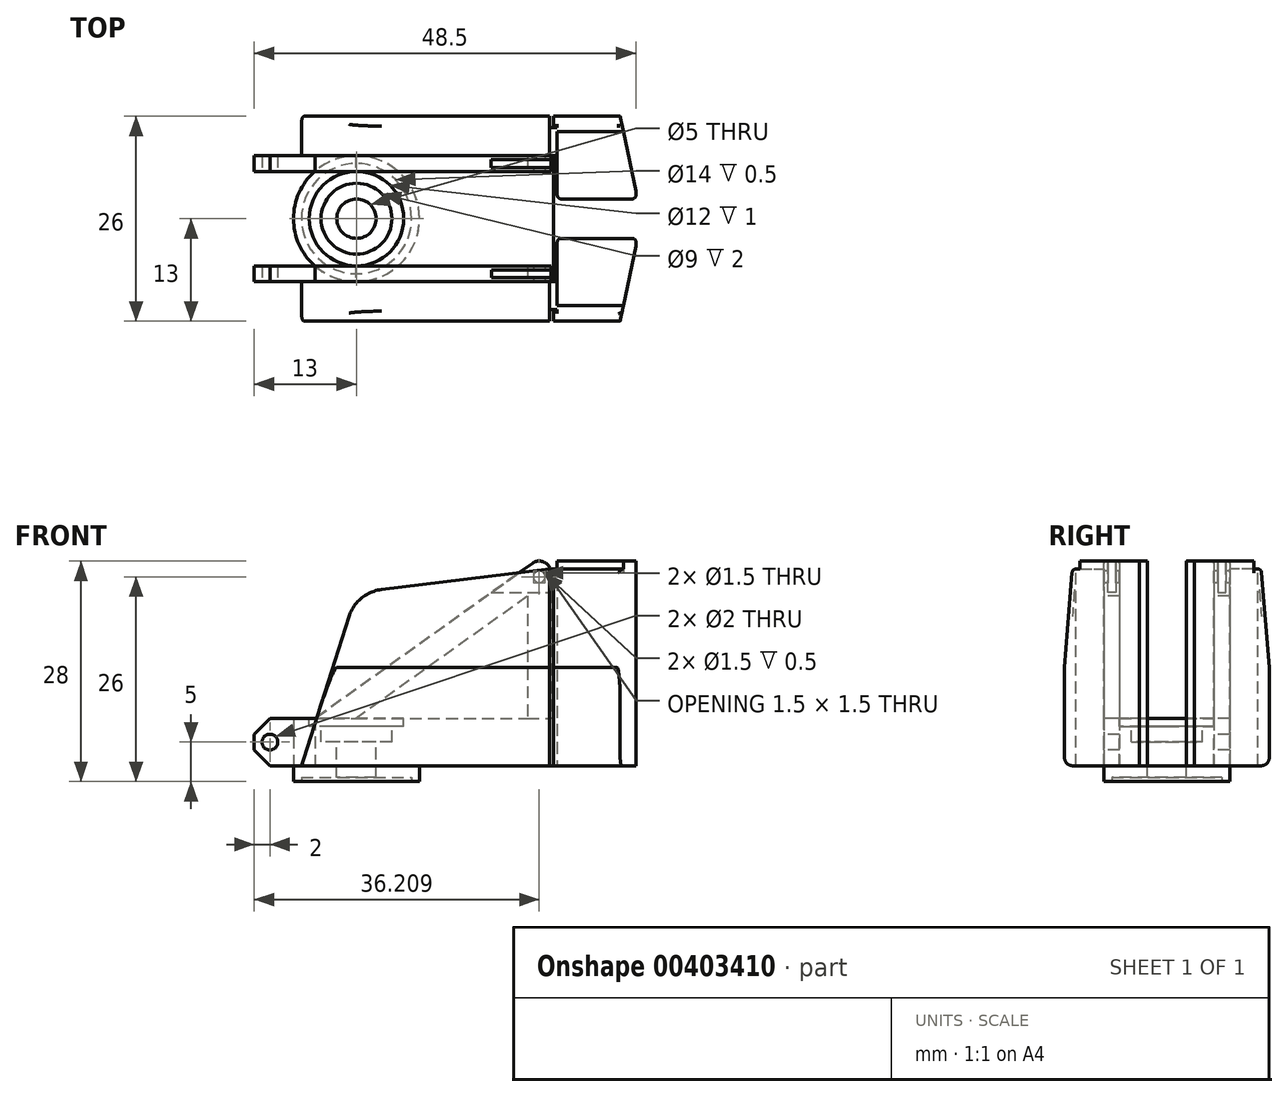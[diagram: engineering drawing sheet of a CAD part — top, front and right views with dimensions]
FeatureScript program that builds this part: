
annotation { "Feature Type Name" : "Feature", "Feature Type Description" : "" }
export const myFeature = defineFeature(function(context is Context, id is Id, definition is map)
    precondition{}
    {
        {
            var Q0;
            Q0=qCreatedBy(makeId("Top.planeOp"),FACE);
            var sketch = newSketch(context, id + "F0", { "sketchPlane" : qUnion([Q0])});
            skCircle(sketch, "E0", {"center": v(0, 0) * mm, "radius": 8 * mm});
            skSolve(sketch);
        }
        {
            var Q0;
            Q0 = qSketchRegion(id + "F0", true);
            extrude(context, id + "F1", {"entities" : qUnion([Q0]), "depth" : 2 * mm});
        }
        {
            var Q0;
            Q0=makeQuery(id+"F1.opExtrude","CAP_FACE",FACE,{"disambiguationData":[OSD([sQuery(id+"F0.wireOp",EDGE,"E0")])],"isStart":true});
            var sketch = newSketch(context, id + "F2", { "sketchPlane" : qUnion([Q0])});
            skCircle(sketch, "E1", {"center": v(0, 0) * mm, "radius": 7 * mm});
            skSolve(sketch);
        }
        {
            var Q0;
            Q0 = qSketchRegion(id + "F2", true);
            extrude(context, id + "F3", {"entities" : qUnion([Q0]), "operationType" : NewBodyOperationType.REMOVE, "oppositeDirection" : true, "depth" : 0.5 * mm});
        }
        {
            var Q0;
            Q0=makeQuery(id+"F1.opExtrude","CAP_FACE",FACE,{"disambiguationData":[OSD([sQuery(id+"F0.wireOp",EDGE,"E0")])],"isStart":false});
            var sketch = newSketch(context, id + "F4", { "sketchPlane" : qUnion([Q0])});
            skLineSegment(sketch, "E2", {"start": v(0, 0) * mm, "end": v(0, 6) * mm, "construction": true});
            skLineSegment(sketch, "E3.MirrorCS", {"start": v(0, 0) * mm, "end": v(0, -6) * mm, "construction": true});
            skLineSegment(sketch, "E4", {"start": v(-8, 0) * mm, "end": v(-13, 0) * mm, "construction": true});
            skLineSegment(sketch, "E5", {"start": v(-5.3, 6) * mm, "end": v(-13, 6) * mm});
            skLineSegment(sketch, "E6", {"start": v(-13, 6) * mm, "end": v(-13, 8) * mm});
            skLineSegment(sketch, "E7", {"start": v(-13, 8) * mm, "end": v(0, 8) * mm});
            skLineSegment(sketch, "E8", {"start": v(0, 8) * mm, "end": v(0, 6) * mm});
            skLineSegment(sketch, "E9.MirrorCS", {"start": v(-5.3, -6) * mm, "end": v(-13, -6) * mm});
            skLineSegment(sketch, "E10.MirrorCS", {"start": v(-13, -6) * mm, "end": v(-13, -8) * mm});
            skLineSegment(sketch, "E11.MirrorCS", {"start": v(-13, -8) * mm, "end": v(0, -8) * mm});
            skLineSegment(sketch, "E12.MirrorCS", {"start": v(0, -8) * mm, "end": v(0, -6) * mm});
            skArc(sketch, "E13", {"start": v(-5.3, -6) * mm, "mid": v(-8, 0) * mm, "end": v(-5.3, 6) * mm});
            skPoint(sketch, "E14.orphan", {"position": v(0, -6) * mm});
            skArc(sketch, "E15", {"start": v(0, -8) * mm, "mid": v(8, 0) * mm, "end": v(0, 8) * mm});
            skLineSegment(sketch, "E16", {"start": v(0, 8) * mm, "end": v(25, 8) * mm});
            skLineSegment(sketch, "E17", {"start": v(25, 8) * mm, "end": v(25, -8) * mm});
            skLineSegment(sketch, "E18", {"start": v(25, -8) * mm, "end": v(0, -8) * mm});
            skSolve(sketch);
        }
        {
            var Q0;
            Q0 = qSketchRegion(id + "F4", true);
            extrude(context, id + "F5", {"entities" : qUnion([Q0]), "operationType" : NewBodyOperationType.ADD, "depth" : 6 * mm});
        }
        {
            var Q0;
            Q0=makeQuery(id+"F5.opExtrude","SWEPT_FACE",FACE,{"disambiguationData":[OSD([sQuery(id+"F4.wireOp",EDGE,"E11.MirrorCS"),sQuery(id+"F4.wireOp",EDGE,"E18")])]});
            var sketch = newSketch(context, id + "F6", { "sketchPlane" : qUnion([Q0])});
            skLineSegment(sketch, "E19", {"start": v(-13, 5) * mm, "end": v(-11, 5) * mm, "construction": true});
            skCircle(sketch, "E20", {"center": v(-11, 5) * mm, "radius": 1 * mm});
            skLineSegment(sketch, "E21", {"start": v(-13, 6) * mm, "end": v(-9.76, 6) * mm, "construction": true});
            skLineSegment(sketch, "E22", {"start": v(-11, 8) * mm, "end": v(-13, 6) * mm});
            skLineSegment(sketch, "E23.MirrorCS", {"start": v(-11, 2) * mm, "end": v(-13, 4) * mm});
            skSolve(sketch);
        }
        {
            var Q0;
            {var subQ0=sQuery(id+"F6.wireOp",EDGE,"E22");Q0=makeQuery(id+"F6.imprint","IMPRINT",FACE,{"disambiguationData":[TD([[makeQuery(id+"F6.imprint","IMPRINT",EDGE,{"derivedFrom":subQ0}),-1.0]])]});}
            var Q1;
            {var subQ0=sQuery(id+"F6.wireOp",EDGE,"E23.MirrorCS");Q1=makeQuery(id+"F6.imprint","IMPRINT",FACE,{"disambiguationData":[TD([[makeQuery(id+"F6.imprint","IMPRINT",EDGE,{"derivedFrom":subQ0}),1.0]])]});}
            var Q2;
            Q2=makeQuery(id+"F6.imprint","IMPRINT",FACE,{"disambiguationData":[TD([[makeQuery(id+"F6.imprint","IMPRINT",EDGE,{"derivedFrom":sQuery(id+"F6.wireOp",EDGE,"E20")}),1.0]])]});
            extrude(context, id + "F7", {"entities" : qUnion([Q0, Q1, Q2]), "operationType" : NewBodyOperationType.REMOVE, "oppositeDirection" : true, "depth" : 25 * mm});
        }
        {
            var Q0;
            Q0=makeQuery(id+"F5.opExtrude","CAP_FACE",FACE,{"disambiguationData":[OSD([sQuery(id+"F4.wireOp",EDGE,"E5"),sQuery(id+"F4.wireOp",EDGE,"E6"),sQuery(id+"F4.wireOp",EDGE,"E7"),sQuery(id+"F4.wireOp",EDGE,"E9.MirrorCS"),sQuery(id+"F4.wireOp",EDGE,"E10.MirrorCS"),sQuery(id+"F4.wireOp",EDGE,"E11.MirrorCS"),sQuery(id+"F4.wireOp",EDGE,"E13"),sQuery(id+"F4.wireOp",EDGE,"E16"),sQuery(id+"F4.wireOp",EDGE,"E17"),sQuery(id+"F4.wireOp",EDGE,"E18")])],"isStart":false});
            var sketch = newSketch(context, id + "F8", { "sketchPlane" : qUnion([Q0])});
            skCircle(sketch, "E24", {"center": v(0, 0) * mm, "radius": 6 * mm});
            skSolve(sketch);
        }
        {
            var Q0;
            Q0=makeQuery(id+"F8.imprint","IMPRINT",FACE,{"disambiguationData":[TD([[makeQuery(id+"F8.imprint","IMPRINT",EDGE,{"derivedFrom":sQuery(id+"F8.wireOp",EDGE,"E24")}),1.0]])]});
            extrude(context, id + "F9", {"entities" : qUnion([Q0]), "operationType" : NewBodyOperationType.REMOVE, "oppositeDirection" : true, "depth" : 1 * mm});
        }
        {
            var Q0;
            Q0=makeQuery(id+"F9.boolean.opBoolean","COPY",FACE,{"derivedFrom":makeQuery(id+"F9.opExtrude","CAP_FACE",FACE,{"disambiguationData":[OSD([sQuery(id+"F8.wireOp",EDGE,"E24")])],"isStart":false})});
            var sketch = newSketch(context, id + "F10", { "sketchPlane" : qUnion([Q0])});
            skCircle(sketch, "E25", {"center": v(0, 0) * mm, "radius": 2.5 * mm});
            skSolve(sketch);
        }
        {
            var Q0;
            Q0=makeQuery(id+"F10.imprint","IMPRINT",FACE,{"disambiguationData":[TD([[makeQuery(id+"F10.imprint","IMPRINT",EDGE,{"derivedFrom":sQuery(id+"F10.wireOp",EDGE,"E25")}),1.0]])]});
            extrude(context, id + "F11", {"entities" : qUnion([Q0]), "operationType" : NewBodyOperationType.REMOVE, "oppositeDirection" : true, "depth" : 25 * mm});
        }
        {
            var Q0;
            Q0=makeQuery(id+"F5.opExtrude","CAP_FACE",FACE,{"disambiguationData":[OSD([sQuery(id+"F4.wireOp",EDGE,"E5"),sQuery(id+"F4.wireOp",EDGE,"E6"),sQuery(id+"F4.wireOp",EDGE,"E7"),sQuery(id+"F4.wireOp",EDGE,"E9.MirrorCS"),sQuery(id+"F4.wireOp",EDGE,"E10.MirrorCS"),sQuery(id+"F4.wireOp",EDGE,"E11.MirrorCS"),sQuery(id+"F4.wireOp",EDGE,"E13"),sQuery(id+"F4.wireOp",EDGE,"E16"),sQuery(id+"F4.wireOp",EDGE,"E17"),sQuery(id+"F4.wireOp",EDGE,"E18")])],"isStart":false});
            var sketch = newSketch(context, id + "F12", { "sketchPlane" : qUnion([Q0])});
            skLineSegment(sketch, "E26", {"start": v(-5.3, 6) * mm, "end": v(24.7, 6) * mm});
            skLineSegment(sketch, "E27", {"start": v(-5.3, 6) * mm, "end": v(-5.3, 8) * mm});
            skLineSegment(sketch, "E28", {"start": v(-5.3, 8) * mm, "end": v(24.7, 8) * mm});
            skLineSegment(sketch, "E29", {"start": v(24.7, 8) * mm, "end": v(24.7, 6) * mm});
            skLineSegment(sketch, "E30.MirrorCS", {"start": v(-5.3, -6) * mm, "end": v(24.7, -6) * mm});
            skLineSegment(sketch, "E31.MirrorCS", {"start": v(-5.3, -6) * mm, "end": v(-5.3, -8) * mm});
            skLineSegment(sketch, "E32.MirrorCS", {"start": v(-5.3, -8) * mm, "end": v(24.7, -8) * mm});
            skLineSegment(sketch, "E33.MirrorCS", {"start": v(24.7, -8) * mm, "end": v(24.7, -6) * mm});
            skSolve(sketch);
        }
        {
            var Q0;
            {var subQ0=sQuery(id+"F12.wireOp",EDGE,"E27");Q0=makeQuery(id+"F12.imprint","IMPRINT",FACE,{"disambiguationData":[TD([[makeQuery(id+"F12.imprint","IMPRINT",EDGE,{"derivedFrom":subQ0}),-1.0]])]});}
            var Q1;
            {var subQ0=sQuery(id+"F12.wireOp",EDGE,"E31.MirrorCS");Q1=makeQuery(id+"F12.imprint","IMPRINT",FACE,{"disambiguationData":[TD([[makeQuery(id+"F12.imprint","IMPRINT",EDGE,{"derivedFrom":subQ0}),1.0]])]});}
            extrude(context, id + "F13", {"entities" : qUnion([Q0, Q1]), "operationType" : NewBodyOperationType.ADD, "depth" : 20 * mm});
        }
        {
            var Q0;
            Q0=makeQuery(id+"F13.boolean.opBoolean","MERGE",FACE,{"derivedFrom":[makeQuery(id+"F5.opExtrude","SWEPT_FACE",FACE,{"disambiguationData":[OSD([sQuery(id+"F4.wireOp",EDGE,"E11.MirrorCS"),sQuery(id+"F4.wireOp",EDGE,"E18")])]}),makeQuery(id+"F13.opExtrude","SWEPT_FACE",FACE,{"disambiguationData":[OSD([sQuery(id+"F12.wireOp",EDGE,"E32.MirrorCS")])]})]});
            var sketch = newSketch(context, id + "F14", { "sketchPlane" : qUnion([Q0])});
            skLineSegment(sketch, "E34", {"start": v(24.7, 28) * mm, "end": v(21.7, 28) * mm, "construction": true});
            skLineSegment(sketch, "E35", {"start": v(23.2, 28) * mm, "end": v(23.2, 26.5) * mm, "construction": true});
            skArc(sketch, "E36", {"start": v(24.7, 26.5) * mm, "mid": v(23.9, 27.83) * mm, "end": v(22.34, 27.72) * mm});
            skLineSegment(sketch, "E37", {"start": v(-5.3, 8) * mm, "end": v(22.34, 27.72) * mm});
            skPoint(sketch, "E37.endSnap0", {"position": v(22.34, 27.72) * mm});
            skLineSegment(sketch, "E38", {"start": v(-5.3, 8) * mm, "end": v(24.7, 8) * mm, "construction": true});
            skLineSegment(sketch, "E39", {"start": v(21.7, 23.59) * mm, "end": v(-0.13, 8) * mm});
            skLineSegment(sketch, "E40", {"start": v(21.7, 8) * mm, "end": v(21.7, 23.59) * mm});
            skLineSegment(sketch, "E41", {"start": v(23.2, 26.5) * mm, "end": v(23.2, 26) * mm, "construction": true});
            skCircle(sketch, "E42", {"center": v(23.2, 26) * mm, "radius": 0.75 * mm});
            skLineSegment(sketch, "E43", {"start": v(-0.13, 8) * mm, "end": v(21.7, 8) * mm});
            skSolve(sketch);
        }
        {
            var Q0;
            {var subQ0=sQuery(id+"F14.wireOp",EDGE,"E37");Q0=makeQuery(id+"F14.imprint","IMPRINT",FACE,{"disambiguationData":[TD([[makeQuery(id+"F14.imprint","IMPRINT",EDGE,{"derivedFrom":subQ0}),1.0]])]});}
            var Q1;
            Q1=makeQuery(id+"F14.imprint","IMPRINT",FACE,{"disambiguationData":[TD([[makeQuery(id+"F14.imprint","IMPRINT",EDGE,{"derivedFrom":sQuery(id+"F14.wireOp",EDGE,"E39")}),1.0]])]});
            var Q2;
            Q2=makeQuery(id+"F14.imprint","IMPRINT",FACE,{"disambiguationData":[TD([[makeQuery(id+"F14.imprint","IMPRINT",EDGE,{"derivedFrom":sQuery(id+"F14.wireOp",EDGE,"E42")}),1.0]])]});
            var Q3;
            {var subQ0=sQuery(id+"F14.wireOp",EDGE,"E36");var subQ1=sQuery(id+"F12.wireOp",EDGE,"E32.MirrorCS");var subQ4=makeQuery(id+"F13.opExtrude","CAP_EDGE",EDGE,{"disambiguationData":[OSD([subQ1])],"isStart":false});var subQ5=makeQuery(id+"F14.imprint","INTERSECT",VERTEX,{"derivedFrom":[subQ4,subQ0]});Q3=makeQuery(id+"F14.imprint","IMPRINT",FACE,{"disambiguationData":[TD([[makeQuery(id+"F14.imprint","IMPRINT",EDGE,{"disambiguationData":[TD([[subQ5,1.0]])],"derivedFrom":subQ0}),-1.0]])]});}
            extrude(context, id + "F15", {"entities" : qUnion([Q0, Q1, Q2, Q3]), "operationType" : NewBodyOperationType.REMOVE, "oppositeDirection" : true, "depth" : 25 * mm});
        }
        {
            var Q0;
            {var subQ0=sQuery(id+"F4.wireOp",EDGE,"E18");var subQ1=sQuery(id+"F4.wireOp",EDGE,"E11.MirrorCS");var subQ2=sQuery(id+"F4.wireOp",EDGE,"E16");var subQ3=sQuery(id+"F4.wireOp",EDGE,"E7");var subQ4=sQuery(id+"F4.wireOp",EDGE,"E17");var subQ5=sQuery(id+"F4.wireOp",EDGE,"E13");var subQ6=makeQuery(id+"F5.opExtrude","CAP_FACE",FACE,{"disambiguationData":[OSD([sQuery(id+"F4.wireOp",EDGE,"E5"),sQuery(id+"F4.wireOp",EDGE,"E6"),subQ3,sQuery(id+"F4.wireOp",EDGE,"E9.MirrorCS"),sQuery(id+"F4.wireOp",EDGE,"E10.MirrorCS"),subQ1,subQ5,subQ2,subQ4,subQ0])],"isStart":true});Q0=makeQuery(id+"F5.boolean.opBoolean","SPLIT",FACE,{"disambiguationData":[TD([makeQuery(id+"F5.opExtrude","SWEPT_FACE",FACE,{"disambiguationData":[OSD([subQ4])]})])],"derivedFrom":subQ6});}
            var sketch = newSketch(context, id + "F16", { "sketchPlane" : qUnion([Q0])});
            skLineSegment(sketch, "E44", {"start": v(0, 0) * mm, "end": v(-7, 0) * mm, "construction": true});
            skPoint(sketch, "E44.endSnap0", {"position": v(8, 0) * mm});
            skLineSegment(sketch, "E45", {"start": v(-7, 0) * mm, "end": v(-7, 8) * mm, "construction": true});
            skLineSegment(sketch, "E46", {"start": v(-7, 8) * mm, "end": v(-7, 13) * mm});
            skLineSegment(sketch, "E47", {"start": v(-7, 13) * mm, "end": v(24.5, 13) * mm});
            skLineSegment(sketch, "E48", {"start": v(24.5, 13) * mm, "end": v(24.5, 8) * mm});
            skLineSegment(sketch, "E49", {"start": v(24.5, 8) * mm, "end": v(-7, 8) * mm});
            skLineSegment(sketch, "E50.MirrorCS", {"start": v(24.5, -8) * mm, "end": v(-7, -8) * mm});
            skLineSegment(sketch, "E51.MirrorCS", {"start": v(-7, -8) * mm, "end": v(-7, -13) * mm});
            skLineSegment(sketch, "E52.MirrorCS", {"start": v(-7, -13) * mm, "end": v(24.5, -13) * mm});
            skLineSegment(sketch, "E53.MirrorCS", {"start": v(24.5, -13) * mm, "end": v(24.5, -8) * mm});
            skSolve(sketch);
        }
        {
            var Q0;
            Q0 = qSketchRegion(id + "F16", true);
            extrude(context, id + "F17", {"entities" : qUnion([Q0]), "operationType" : NewBodyOperationType.ADD, "oppositeDirection" : true, "depth" : 25 * mm});
        }
        {
            var Q0;
            Q0=makeQuery(id+"F17.opExtrude","SWEPT_FACE",FACE,{"disambiguationData":[OSD([sQuery(id+"F16.wireOp",EDGE,"E47")])]});
            var sketch = newSketch(context, id + "F18", { "sketchPlane" : qUnion([Q0])});
            skLineSegment(sketch, "E54", {"start": v(-7, 2) * mm, "end": v(-0.97, 20.94) * mm});
            skLineSegment(sketch, "E55", {"start": v(3.18, 24.39) * mm, "end": v(24.5, 27) * mm});
            skLineSegment(sketch, "E56", {"start": v(0, 27) * mm, "end": v(0, 24) * mm, "construction": true});
            skPoint(sketch, "E57.visualSharp", {"position": v(0, 24) * mm});
            skArc(sketch, "E57.filletArc", {"start": v(3.18, 24.39) * mm, "mid": v(0.6, 23.28) * mm, "end": v(-0.97, 20.94) * mm});
            skSolve(sketch);
        }
        {
            var Q0;
            Q0=makeQuery(id+"F18.imprint","IMPRINT",FACE,{"disambiguationData":[TD([[makeQuery(id+"F18.imprint","IMPRINT",EDGE,{"derivedFrom":sQuery(id+"F18.wireOp",EDGE,"E54")}),1.0]])]});
            extrude(context, id + "F19", {"entities" : qUnion([Q0]), "operationType" : NewBodyOperationType.REMOVE, "oppositeDirection" : true, "depth" : 5 * mm});
        }
        {
            var Q0;
            Q0=makeQuery(id+"F17.opExtrude","SWEPT_FACE",FACE,{"disambiguationData":[OSD([sQuery(id+"F16.wireOp",EDGE,"E48")])]});
            var sketch = newSketch(context, id + "F20", { "sketchPlane" : qUnion([Q0])});
            skLineSegment(sketch, "E58", {"start": v(-13, 14.5) * mm, "end": v(-12, 27) * mm});
            skLineSegment(sketch, "E59", {"start": v(-12, 27) * mm, "end": v(-8, 27) * mm});
            skSolve(sketch);
        }
        {
            var Q0;
            {var subQ0=sQuery(id+"F20.wireOp",EDGE,"E58");Q0=makeQuery(id+"F20.imprint","IMPRINT",FACE,{"disambiguationData":[TD([[makeQuery(id+"F20.imprint","IMPRINT",EDGE,{"derivedFrom":subQ0}),1.0]])]});}
            extrude(context, id + "F21", {"entities" : qUnion([Q0]), "operationType" : NewBodyOperationType.REMOVE, "oppositeDirection" : true, "depth" : 30 * mm});
        }
        {
            var Q0;
            Q0=makeQuery(id+"F21.boolean.opBoolean","INTERSECT",EDGE,{"derivedFrom":[makeQuery(id+"F19.boolean.opBoolean","COPY",FACE,{"derivedFrom":makeQuery(id+"F19.opExtrude","SWEPT_FACE",FACE,{"disambiguationData":[OSD([sQuery(id+"F18.wireOp",EDGE,"E55")])]})}),makeQuery(id+"F21.opExtrude","SWEPT_FACE",FACE,{"disambiguationData":[OSD([sQuery(id+"F20.wireOp",EDGE,"E58")])]})]});
            var Q1;
            Q1=makeQuery(id+"F21.boolean.opBoolean","INTERSECT",EDGE,{"derivedFrom":[makeQuery(id+"F19.boolean.opBoolean","COPY",FACE,{"derivedFrom":makeQuery(id+"F19.opExtrude","SWEPT_FACE",FACE,{"disambiguationData":[OSD([sQuery(id+"F18.wireOp",EDGE,"E57.filletArc")])]})}),makeQuery(id+"F21.opExtrude","SWEPT_FACE",FACE,{"disambiguationData":[OSD([sQuery(id+"F20.wireOp",EDGE,"E58")])]})]});
            fillet(context, id + "F22", {"entities" : qUnion([Q0, Q1]), "radius" : 0.5 * mm, "tangentPropagation" : true, "allowEdgeOverflow" : false});
        }
        {
            var Q0;
            Q0=makeQuery(id+"F17.opExtrude","SWEPT_FACE",FACE,{"disambiguationData":[OSD([sQuery(id+"F16.wireOp",EDGE,"E52.MirrorCS")])]});
            var sketch = newSketch(context, id + "F23", { "sketchPlane" : qUnion([Q0])});
            skLineSegment(sketch, "E60", {"start": v(7, 2) * mm, "end": v(0.97, 20.94) * mm});
            skLineSegment(sketch, "E61", {"start": v(-3.18, 24.39) * mm, "end": v(-24.5, 27) * mm});
            skLineSegment(sketch, "E62", {"start": v(0, 24) * mm, "end": v(0, 27) * mm, "construction": true});
            skPoint(sketch, "E63.visualSharp", {"position": v(0, 24) * mm});
            skArc(sketch, "E63.filletArc", {"start": v(0.97, 20.94) * mm, "mid": v(-0.6, 23.28) * mm, "end": v(-3.18, 24.39) * mm});
            skSolve(sketch);
        }
        {
            var Q0;
            Q0=makeQuery(id+"F23.imprint","IMPRINT",FACE,{"disambiguationData":[TD([[makeQuery(id+"F23.imprint","IMPRINT",EDGE,{"derivedFrom":sQuery(id+"F23.wireOp",EDGE,"E60")}),-1.0]])]});
            extrude(context, id + "F24", {"entities" : qUnion([Q0]), "operationType" : NewBodyOperationType.REMOVE, "oppositeDirection" : true, "depth" : 5 * mm});
        }
        {
            var Q0;
            Q0=makeQuery(id+"F17.opExtrude","SWEPT_FACE",FACE,{"disambiguationData":[OSD([sQuery(id+"F16.wireOp",EDGE,"E53.MirrorCS")])]});
            var sketch = newSketch(context, id + "F25", { "sketchPlane" : qUnion([Q0])});
            skLineSegment(sketch, "E64", {"start": v(13, 14.5) * mm, "end": v(12, 27) * mm});
            skLineSegment(sketch, "E65", {"start": v(12, 27) * mm, "end": v(8, 27) * mm});
            skSolve(sketch);
        }
        {
            var Q0;
            {var subQ0=sQuery(id+"F25.wireOp",EDGE,"E64");Q0=makeQuery(id+"F25.imprint","IMPRINT",FACE,{"disambiguationData":[TD([[makeQuery(id+"F25.imprint","IMPRINT",EDGE,{"derivedFrom":subQ0}),-1.0]])]});}
            extrude(context, id + "F26", {"entities" : qUnion([Q0]), "operationType" : NewBodyOperationType.REMOVE, "oppositeDirection" : true, "depth" : 30 * mm});
        }
        {
            var Q0;
            Q0=makeQuery(id+"F26.boolean.opBoolean","INTERSECT",EDGE,{"derivedFrom":[makeQuery(id+"F24.boolean.opBoolean","COPY",FACE,{"derivedFrom":makeQuery(id+"F24.opExtrude","SWEPT_FACE",FACE,{"disambiguationData":[OSD([sQuery(id+"F23.wireOp",EDGE,"E61")])]})}),makeQuery(id+"F26.opExtrude","SWEPT_FACE",FACE,{"disambiguationData":[OSD([sQuery(id+"F25.wireOp",EDGE,"E64")])]})]});
            var Q1;
            Q1=makeQuery(id+"F26.boolean.opBoolean","INTERSECT",EDGE,{"derivedFrom":[makeQuery(id+"F24.boolean.opBoolean","COPY",FACE,{"derivedFrom":makeQuery(id+"F24.opExtrude","SWEPT_FACE",FACE,{"disambiguationData":[OSD([sQuery(id+"F23.wireOp",EDGE,"E63.filletArc")])]})}),makeQuery(id+"F26.opExtrude","SWEPT_FACE",FACE,{"disambiguationData":[OSD([sQuery(id+"F25.wireOp",EDGE,"E64")])]})]});
            fillet(context, id + "F27", {"entities" : qUnion([Q0, Q1]), "radius" : 0.5 * mm, "tangentPropagation" : true, "allowEdgeOverflow" : false});
        }
        {
            var Q0;
            Q0=makeQuery(id+"F13.opExtrude","SWEPT_FACE",FACE,{"disambiguationData":[OSD([sQuery(id+"F12.wireOp",EDGE,"E33.MirrorCS")])]});
            var sketch = newSketch(context, id + "F28", { "sketchPlane" : qUnion([Q0])});
            skLineSegment(sketch, "E66", {"start": v(-7, 26.5) * mm, "end": v(-6.5, 26.5) * mm, "construction": true});
            skLineSegment(sketch, "E67", {"start": v(-7, 26.5) * mm, "end": v(-7.5, 26.5) * mm, "construction": true});
            skLineSegment(sketch, "E68", {"start": v(-7.5, 26.5) * mm, "end": v(-7.5, 28.04) * mm});
            skLineSegment(sketch, "E69", {"start": v(-7.5, 28.04) * mm, "end": v(-6.5, 28.04) * mm});
            skLineSegment(sketch, "E70", {"start": v(-6.5, 28.04) * mm, "end": v(-6.5, 24.04) * mm});
            skLineSegment(sketch, "E71", {"start": v(-6.5, 24.04) * mm, "end": v(-7.5, 24.04) * mm});
            skLineSegment(sketch, "E72", {"start": v(-7.5, 24.04) * mm, "end": v(-7.5, 26.5) * mm});
            skSolve(sketch);
        }
        {
            var Q0;
            {var subQ0=sQuery(id+"F28.wireOp",EDGE,"E68");Q0=makeQuery(id+"F28.imprint","IMPRINT",FACE,{"disambiguationData":[TD([[makeQuery(id+"F28.imprint","IMPRINT",EDGE,{"derivedFrom":subQ0}),-1.0]])]});}
            var Q1;
            {var subQ0=sQuery(id+"F28.wireOp",EDGE,"E71");Q1=makeQuery(id+"F28.imprint","IMPRINT",FACE,{"disambiguationData":[TD([[makeQuery(id+"F28.imprint","IMPRINT",EDGE,{"derivedFrom":subQ0}),-1.0]])]});}
            extrude(context, id + "F29", {"entities" : qUnion([Q0, Q1]), "operationType" : NewBodyOperationType.REMOVE, "oppositeDirection" : true, "depth" : 25 * mm});
        }
        {
            var Q0;
            Q0=makeQuery(id+"F13.opExtrude","SWEPT_FACE",FACE,{"disambiguationData":[OSD([sQuery(id+"F12.wireOp",EDGE,"E29")])]});
            var sketch = newSketch(context, id + "F30", { "sketchPlane" : qUnion([Q0])});
            skLineSegment(sketch, "E73", {"start": v(7, 26.5) * mm, "end": v(7.5, 26.5) * mm, "construction": true});
            skLineSegment(sketch, "E74", {"start": v(7, 26.5) * mm, "end": v(6.5, 26.5) * mm, "construction": true});
            skLineSegment(sketch, "E75", {"start": v(7.5, 26.5) * mm, "end": v(7.5, 28.27) * mm});
            skLineSegment(sketch, "E76", {"start": v(7.5, 28.27) * mm, "end": v(6.5, 28.27) * mm});
            skLineSegment(sketch, "E77", {"start": v(6.5, 28.27) * mm, "end": v(6.5, 26.5) * mm});
            skLineSegment(sketch, "E78", {"start": v(6.5, 26.5) * mm, "end": v(6.5, 24) * mm});
            skLineSegment(sketch, "E79", {"start": v(6.5, 24) * mm, "end": v(7.5, 24) * mm});
            skLineSegment(sketch, "E80", {"start": v(7.5, 24) * mm, "end": v(7.5, 26.5) * mm});
            skSolve(sketch);
        }
        {
            var Q0;
            Q0 = qSketchRegion(id + "F30", true);
            extrude(context, id + "F31", {"entities" : qUnion([Q0]), "operationType" : NewBodyOperationType.REMOVE, "oppositeDirection" : true, "depth" : 25 * mm});
        }
        {
            var Q0;
            Q0=makeQuery(id+"F9.boolean.opBoolean","COPY",FACE,{"derivedFrom":makeQuery(id+"F9.opExtrude","CAP_FACE",FACE,{"disambiguationData":[OSD([sQuery(id+"F8.wireOp",EDGE,"E24")])],"isStart":false})});
            var sketch = newSketch(context, id + "F32", { "sketchPlane" : qUnion([Q0])});
            skCircle(sketch, "E81", {"center": v(0, 0) * mm, "radius": 4.5 * mm});
            skSolve(sketch);
        }
        {
            var Q0;
            Q0 = qSketchRegion(id + "F32", true);
            extrude(context, id + "F33", {"entities" : qUnion([Q0]), "operationType" : NewBodyOperationType.REMOVE, "oppositeDirection" : true, "depth" : 2 * mm});
        }
        {
            var Q0;
            Q0=makeQuery(id+"F17.opExtrude","SWEPT_FACE",FACE,{"disambiguationData":[OSD([sQuery(id+"F16.wireOp",EDGE,"E48")])]});
            var sketch = newSketch(context, id + "F34", { "sketchPlane" : qUnion([Q0])});
            skLineSegment(sketch, "E82", {"start": v(-13, 2) * mm, "end": v(-13, 14.5) * mm});
            skLineSegment(sketch, "E83", {"start": v(-13, 14.5) * mm, "end": v(-12.04, 26.5) * mm});
            skLineSegment(sketch, "E84", {"start": v(-12, 26.56) * mm, "end": v(-11.54, 27) * mm});
            skLineSegment(sketch, "E85", {"start": v(-11.54, 27) * mm, "end": v(-8, 27) * mm});
            skLineSegment(sketch, "E86", {"start": v(-8, 27) * mm, "end": v(-8, 2) * mm});
            skLineSegment(sketch, "E87", {"start": v(-8, 2) * mm, "end": v(-13, 2) * mm});
            skPoint(sketch, "E88.visualSharp", {"position": v(-12.04, 26.54) * mm});
            skArc(sketch, "E88.filletArc", {"start": v(-12, 26.56) * mm, "mid": v(-12.03, 26.53) * mm, "end": v(-12.04, 26.5) * mm});
            skArc(sketch, "E89", {"start": v(-12.04, 26.54) * mm, "mid": v(-11.88, 26.86) * mm, "end": v(-11.54, 27) * mm});
            skSolve(sketch);
        }
        {
            var Q0;
            Q0 = qSketchRegion(id + "F34", true);
            var Q1;
            {var subQ0=sQuery(id+"F34.wireOp",EDGE,"E88.filletArc");Q1=makeQuery(id+"F34.imprint","IMPRINT",FACE,{"disambiguationData":[TD([[makeQuery(id+"F34.imprint","IMPRINT",EDGE,{"derivedFrom":subQ0}),-1.0]])]});}
            extrude(context, id + "F35", {"entities" : qUnion([Q0, Q1]), "depth" : 1 * mm});
        }
        {
            var Q0;
            Q0=makeQuery(id+"F35.opExtrude","SWEPT_BODY",BODY,{"disambiguationData":[OSD([sQuery(id+"F34.wireOp",EDGE,"E82"),sQuery(id+"F34.wireOp",EDGE,"E83"),sQuery(id+"F34.wireOp",EDGE,"E84"),sQuery(id+"F34.wireOp",EDGE,"E85"),sQuery(id+"F34.wireOp",EDGE,"E86"),sQuery(id+"F34.wireOp",EDGE,"E87"),sQuery(id+"F34.wireOp",EDGE,"E88.filletArc")])]});
            var Q1;
            Q1=qCreatedBy(makeId("Front.planeOp"),FACE);
            mirror(context, id + "F36", {"operationType" : NewBodyOperationType.ADD, "entities" : qUnion([Q0]), "mirrorPlane" : qUnion([Q1])});
        }
        {
            var Q0;
            Q0=makeQuery(id+"F35.opExtrude","CAP_FACE",FACE,{"disambiguationData":[OSD([sQuery(id+"F20.wireOp",EDGE,"E58"),sQuery(id+"F34.wireOp",EDGE,"E82"),sQuery(id+"F34.wireOp",EDGE,"E83"),sQuery(id+"F34.wireOp",EDGE,"E84"),sQuery(id+"F34.wireOp",EDGE,"E85"),sQuery(id+"F34.wireOp",EDGE,"E86"),sQuery(id+"F34.wireOp",EDGE,"E87"),sQuery(id+"F34.wireOp",EDGE,"E89")])],"isStart":false});
            var sketch = newSketch(context, id + "F37", { "sketchPlane" : qUnion([Q0])});
            skLineSegment(sketch, "E90", {"start": v(-13, 2) * mm, "end": v(-13, 14.5) * mm});
            skLineSegment(sketch, "E91", {"start": v(-13, 14.5) * mm, "end": v(-12.04, 26.54) * mm});
            skLineSegment(sketch, "E92", {"start": v(-11.54, 27) * mm, "end": v(11.54, 27) * mm});
            skLineSegment(sketch, "E93.0", {"start": v(13, 14.5) * mm, "end": v(12.04, 26.54) * mm});
            skLineSegment(sketch, "E94.0", {"start": v(13, 14.5) * mm, "end": v(13, 2) * mm});
            skLineSegment(sketch, "E95", {"start": v(12.04, 26.54) * mm, "end": v(13, 14.5) * mm});
            skLineSegment(sketch, "E96", {"start": v(13, 2) * mm, "end": v(-13, 2) * mm});
            skPoint(sketch, "E97.visualSharp", {"position": v(-12, 27) * mm});
            skArc(sketch, "E97.filletArc", {"start": v(-11.54, 27) * mm, "mid": v(-11.88, 26.87) * mm, "end": v(-12.04, 26.54) * mm});
            skPoint(sketch, "E98.visualSharp", {"position": v(12, 27) * mm});
            skArc(sketch, "E98.filletArc", {"start": v(12.04, 26.54) * mm, "mid": v(11.88, 26.87) * mm, "end": v(11.54, 27) * mm});
            skSolve(sketch);
        }
        {
            var Q0;
            Q0 = qSketchRegion(id + "F37", true);
            extrude(context, id + "F38", {"entities" : qUnion([Q0]), "operationType" : NewBodyOperationType.ADD, "depth" : 10 * mm});
        }
        {
            var Q0;
            {var subQ0=makeQuery(id+"F35.opExtrude","SWEPT_FACE",FACE,{"disambiguationData":[OSD([sQuery(id+"F34.wireOp",EDGE,"E87")])]});var subQ1=sQuery(id+"F4.wireOp",EDGE,"E9.MirrorCS");var subQ3=sQuery(id+"F4.wireOp",EDGE,"E10.MirrorCS");var subQ4=sQuery(id+"F4.wireOp",EDGE,"E18");var subQ5=sQuery(id+"F4.wireOp",EDGE,"E17");var subQ6=sQuery(id+"F4.wireOp",EDGE,"E16");var subQ7=sQuery(id+"F4.wireOp",EDGE,"E13");var subQ8=sQuery(id+"F4.wireOp",EDGE,"E11.MirrorCS");var subQ9=sQuery(id+"F4.wireOp",EDGE,"E7");var subQ10=sQuery(id+"F4.wireOp",EDGE,"E6");var subQ11=sQuery(id+"F4.wireOp",EDGE,"E5");var subQ12=makeQuery(id+"F5.opExtrude","CAP_FACE",FACE,{"disambiguationData":[OSD([subQ11,subQ10,subQ9,subQ1,subQ3,subQ8,subQ7,subQ6,subQ5,subQ4])],"isStart":true});Q0=makeQuery(id+"F38.boolean.opBoolean","MERGE",FACE,{"derivedFrom":[makeQuery(id+"F36.boolean.opBoolean","MERGE",FACE,{"derivedFrom":[makeQuery(id+"F17.boolean.opBoolean","MERGE",FACE,{"derivedFrom":[makeQuery(id+"F5.boolean.opBoolean","SPLIT",FACE,{"disambiguationData":[TD([makeQuery(id+"F5.opExtrude","SWEPT_FACE",FACE,{"disambiguationData":[OSD([subQ5])]})])],"derivedFrom":subQ12}),makeQuery(id+"F5.boolean.opBoolean","SPLIT",FACE,{"disambiguationData":[TD([makeQuery(id+"F5.opExtrude","SWEPT_FACE",FACE,{"disambiguationData":[OSD([subQ11])]})])],"derivedFrom":subQ12}),makeQuery(id+"F5.boolean.opBoolean","SPLIT",FACE,{"disambiguationData":[TD([makeQuery(id+"F5.opExtrude","SWEPT_FACE",FACE,{"disambiguationData":[OSD([subQ1])]})])],"derivedFrom":subQ12}),makeQuery(id+"F17.opExtrude","CAP_FACE",FACE,{"disambiguationData":[OSD([sQuery(id+"F16.wireOp",EDGE,"E46"),sQuery(id+"F16.wireOp",EDGE,"E47"),sQuery(id+"F16.wireOp",EDGE,"E48"),sQuery(id+"F16.wireOp",EDGE,"E49")])],"isStart":true}),makeQuery(id+"F17.opExtrude","CAP_FACE",FACE,{"disambiguationData":[OSD([sQuery(id+"F16.wireOp",EDGE,"E50.MirrorCS"),sQuery(id+"F16.wireOp",EDGE,"E51.MirrorCS"),sQuery(id+"F16.wireOp",EDGE,"E52.MirrorCS"),sQuery(id+"F16.wireOp",EDGE,"E53.MirrorCS")])],"isStart":true})]}),subQ0,makeQuery(id+"F36.opPattern","COPY",FACE,{"derivedFrom":subQ0,"instanceName":"1"})]}),makeQuery(id+"F38.opExtrude","SWEPT_FACE",FACE,{"disambiguationData":[OSD([sQuery(id+"F37.wireOp",EDGE,"E96")])]})]});}
            var sketch = newSketch(context, id + "F39", { "sketchPlane" : qUnion([Q0])});
            skLineSegment(sketch, "E99", {"start": v(35.5, 13) * mm, "end": v(33.5, 13) * mm, "construction": true});
            skLineSegment(sketch, "E100", {"start": v(33.5, 13) * mm, "end": v(35.5, 3.5) * mm});
            skLineSegment(sketch, "E101", {"start": v(35.5, 3.5) * mm, "end": v(35.5, -3.5) * mm});
            skLineSegment(sketch, "E102", {"start": v(35.5, -3.5) * mm, "end": v(33.5, -13) * mm});
            skLineSegment(sketch, "E103", {"start": v(33.5, 13) * mm, "end": v(35.5, 13) * mm});
            skLineSegment(sketch, "E104", {"start": v(35.5, 13) * mm, "end": v(35.5, -13) * mm});
            skLineSegment(sketch, "E105", {"start": v(35.5, -13) * mm, "end": v(33.5, -13) * mm});
            skSolve(sketch);
        }
        {
            var Q0;
            Q0 = qSketchRegion(id + "F39", true);
            extrude(context, id + "F40", {"entities" : qUnion([Q0]), "operationType" : NewBodyOperationType.REMOVE, "oppositeDirection" : true, "depth" : 25 * mm});
        }
        {
            var Q0;
            Q0=makeQuery(id+"F38.opExtrude","CAP_FACE",FACE,{"disambiguationData":[OSD([sQuery(id+"F37.wireOp",EDGE,"E90"),sQuery(id+"F37.wireOp",EDGE,"E91"),sQuery(id+"F37.wireOp",EDGE,"E92"),sQuery(id+"F37.wireOp",EDGE,"E94.0"),sQuery(id+"F37.wireOp",EDGE,"E95"),sQuery(id+"F37.wireOp",EDGE,"E96"),sQuery(id+"F37.wireOp",EDGE,"E97.filletArc"),sQuery(id+"F37.wireOp",EDGE,"E98.filletArc")])],"isStart":false});
            var sketch = newSketch(context, id + "F41", { "sketchPlane" : qUnion([Q0])});
            skLineSegment(sketch, "E106", {"start": v(0, 2) * mm, "end": v(2.5, 2) * mm, "construction": true});
            skLineSegment(sketch, "E107", {"start": v(2.5, 2) * mm, "end": v(2.5, 27) * mm});
            skLineSegment(sketch, "E108", {"start": v(2.5, 27) * mm, "end": v(-2.5, 27) * mm});
            skLineSegment(sketch, "E109", {"start": v(-2.5, 27) * mm, "end": v(-2.5, 2) * mm});
            skLineSegment(sketch, "E110", {"start": v(-2.5, 2) * mm, "end": v(2.5, 2) * mm});
            skSolve(sketch);
        }
        {
            var Q0;
            Q0 = qSketchRegion(id + "F41", true);
            extrude(context, id + "F42", {"entities" : qUnion([Q0]), "operationType" : NewBodyOperationType.REMOVE, "oppositeDirection" : true, "depth" : 10 * mm});
        }
        {
            var Q0;
            {var subQ5=sQuery(id+"F37.wireOp",EDGE,"E92");var subQ8=sQuery(id+"F12.wireOp",EDGE,"E32.MirrorCS");var subQ14=makeQuery(id+"F35.opExtrude","SWEPT_FACE",FACE,{"disambiguationData":[OSD([sQuery(id+"F34.wireOp",EDGE,"E85")])]});Q0=makeQuery(id+"F42.boolean.opBoolean","SPLIT",FACE,{"disambiguationData":[TD([makeQuery(id+"F13.opExtrude","SWEPT_FACE",FACE,{"disambiguationData":[OSD([subQ8])]})])],"derivedFrom":makeQuery(id+"F38.boolean.opBoolean","MERGE",FACE,{"derivedFrom":[subQ14,makeQuery(id+"F36.opPattern","COPY",FACE,{"derivedFrom":subQ14,"instanceName":"1"}),makeQuery(id+"F38.opExtrude","SWEPT_FACE",FACE,{"disambiguationData":[OSD([subQ5])]})]})});}
            var sketch = newSketch(context, id + "F43", { "sketchPlane" : qUnion([Q0])});
            skLineSegment(sketch, "E111", {"start": v(24.5, -11.54) * mm, "end": v(25, -11.54) * mm});
            skLineSegment(sketch, "E112", {"start": v(25, -11.54) * mm, "end": v(25, -14.07) * mm});
            skLineSegment(sketch, "E113", {"start": v(25, -14.07) * mm, "end": v(24.5, -14.07) * mm});
            skLineSegment(sketch, "E114", {"start": v(24.5, -14.07) * mm, "end": v(24.5, -11.54) * mm});
            skPoint(sketch, "E115", {"position": v(24.75, -11.54) * mm});
            skSolve(sketch);
        }
        {
            var Q0;
            Q0 = qSketchRegion(id + "F43", true);
            extrude(context, id + "F44", {"entities" : qUnion([Q0]), "operationType" : NewBodyOperationType.REMOVE, "oppositeDirection" : true, "depth" : 25 * mm});
        }
        {
            var Q0;
            {var subQ5=sQuery(id+"F37.wireOp",EDGE,"E92");var subQ12=makeQuery(id+"F35.opExtrude","SWEPT_FACE",FACE,{"disambiguationData":[OSD([sQuery(id+"F34.wireOp",EDGE,"E85")])]});Q0=makeQuery(id+"F42.boolean.opBoolean","SPLIT",FACE,{"disambiguationData":[TD([makeQuery(id+"F13.opExtrude","SWEPT_FACE",FACE,{"disambiguationData":[OSD([sQuery(id+"F12.wireOp",EDGE,"E28")])]})])],"derivedFrom":makeQuery(id+"F38.boolean.opBoolean","MERGE",FACE,{"derivedFrom":[subQ12,makeQuery(id+"F36.opPattern","COPY",FACE,{"derivedFrom":subQ12,"instanceName":"1"}),makeQuery(id+"F38.opExtrude","SWEPT_FACE",FACE,{"disambiguationData":[OSD([subQ5])]})]})});}
            var sketch = newSketch(context, id + "F45", { "sketchPlane" : qUnion([Q0])});
            skLineSegment(sketch, "E116", {"start": v(24.5, 11.54) * mm, "end": v(25, 11.54) * mm});
            skLineSegment(sketch, "E117", {"start": v(25, 11.54) * mm, "end": v(25, 14.56) * mm});
            skLineSegment(sketch, "E118", {"start": v(25, 14.56) * mm, "end": v(24.5, 14.56) * mm});
            skLineSegment(sketch, "E119", {"start": v(24.5, 14.56) * mm, "end": v(24.5, 11.54) * mm});
            skSolve(sketch);
        }
        {
            var Q0;
            Q0 = qSketchRegion(id + "F45", true);
            extrude(context, id + "F46", {"entities" : qUnion([Q0]), "operationType" : NewBodyOperationType.REMOVE, "oppositeDirection" : true, "depth" : 25 * mm});
        }
        {
            var Q0;
            {var subQ0=sQuery(id+"F37.wireOp",EDGE,"E90");var subQ1=sQuery(id+"F34.wireOp",EDGE,"E87");var subQ3=sQuery(id+"F16.wireOp",EDGE,"E48");var subQ4=sQuery(id+"F16.wireOp",EDGE,"E47");var subQ5=sQuery(id+"F34.wireOp",EDGE,"E82");var subQ6=sQuery(id+"F37.wireOp",EDGE,"E96");Q0=makeQuery(id+"F44.boolean.opBoolean","SPLIT",EDGE,{"disambiguationData":[TD([makeQuery(id+"F17.opExtrude","SWEPT_FACE",FACE,{"disambiguationData":[OSD([subQ3])]})])],"derivedFrom":makeQuery(id+"F38.boolean.opBoolean","MERGE",EDGE,{"derivedFrom":[makeQuery(id+"F36.boolean.opBoolean","MERGE",EDGE,{"derivedFrom":[makeQuery(id+"F17.opExtrude","CAP_EDGE",EDGE,{"disambiguationData":[OSD([subQ4])],"isStart":true}),makeQuery(id+"F35.opExtrude","SWEPT_EDGE",EDGE,{"disambiguationData":[OSD([subQ5,subQ1])]})]}),makeQuery(id+"F38.opExtrude","SWEPT_EDGE",EDGE,{"disambiguationData":[OSD([subQ0,subQ6])]})]})});}
            var Q1;
            {var subQ0=sQuery(id+"F37.wireOp",EDGE,"E96");var subQ1=sQuery(id+"F37.wireOp",EDGE,"E90");var subQ2=sQuery(id+"F34.wireOp",EDGE,"E87");var subQ4=sQuery(id+"F34.wireOp",EDGE,"E82");var subQ5=sQuery(id+"F16.wireOp",EDGE,"E47");Q1=makeQuery(id+"F44.boolean.opBoolean","SPLIT",EDGE,{"disambiguationData":[TD([makeQuery(id+"F40.boolean.opBoolean","COPY",FACE,{"derivedFrom":makeQuery(id+"F40.opExtrude","SWEPT_FACE",FACE,{"disambiguationData":[OSD([sQuery(id+"F39.wireOp",EDGE,"E100")])]})})])],"derivedFrom":makeQuery(id+"F38.boolean.opBoolean","MERGE",EDGE,{"derivedFrom":[makeQuery(id+"F36.boolean.opBoolean","MERGE",EDGE,{"derivedFrom":[makeQuery(id+"F17.opExtrude","CAP_EDGE",EDGE,{"disambiguationData":[OSD([subQ5])],"isStart":true}),makeQuery(id+"F35.opExtrude","SWEPT_EDGE",EDGE,{"disambiguationData":[OSD([subQ4,subQ2])]})]}),makeQuery(id+"F38.opExtrude","SWEPT_EDGE",EDGE,{"disambiguationData":[OSD([subQ1,subQ0])]})]})});}
            var Q2;
            Q2=makeQuery(id+"F40.boolean.opBoolean","COPY",EDGE,{"derivedFrom":makeQuery(id+"F40.opExtrude","CAP_EDGE",EDGE,{"disambiguationData":[OSD([sQuery(id+"F39.wireOp",EDGE,"E100")])],"isStart":true})});
            var Q3;
            Q3=makeQuery(id+"F40.boolean.opBoolean","COPY",EDGE,{"derivedFrom":makeQuery(id+"F40.opExtrude","CAP_EDGE",EDGE,{"disambiguationData":[OSD([sQuery(id+"F39.wireOp",EDGE,"E102")])],"isStart":true})});
            var Q4;
            {var subQ0=sQuery(id+"F37.wireOp",EDGE,"E96");var subQ1=sQuery(id+"F34.wireOp",EDGE,"E82");var subQ2=sQuery(id+"F34.wireOp",EDGE,"E87");var subQ4=sQuery(id+"F37.wireOp",EDGE,"E94.0");var subQ5=sQuery(id+"F16.wireOp",EDGE,"E52.MirrorCS");Q4=makeQuery(id+"F46.boolean.opBoolean","SPLIT",EDGE,{"disambiguationData":[TD([makeQuery(id+"F40.boolean.opBoolean","COPY",FACE,{"derivedFrom":makeQuery(id+"F40.opExtrude","SWEPT_FACE",FACE,{"disambiguationData":[OSD([sQuery(id+"F39.wireOp",EDGE,"E102")])]})})])],"derivedFrom":makeQuery(id+"F38.boolean.opBoolean","MERGE",EDGE,{"derivedFrom":[makeQuery(id+"F36.boolean.opBoolean","MERGE",EDGE,{"derivedFrom":[makeQuery(id+"F17.opExtrude","CAP_EDGE",EDGE,{"disambiguationData":[OSD([subQ5])],"isStart":true}),makeQuery(id+"F36.opPattern","COPY",EDGE,{"derivedFrom":makeQuery(id+"F35.opExtrude","SWEPT_EDGE",EDGE,{"disambiguationData":[OSD([subQ1,subQ2])]}),"instanceName":"1"})]}),makeQuery(id+"F38.opExtrude","SWEPT_EDGE",EDGE,{"disambiguationData":[OSD([subQ4,subQ0])]})]})});}
            var Q5;
            {var subQ0=sQuery(id+"F34.wireOp",EDGE,"E82");var subQ1=sQuery(id+"F37.wireOp",EDGE,"E96");var subQ2=sQuery(id+"F34.wireOp",EDGE,"E87");var subQ4=sQuery(id+"F16.wireOp",EDGE,"E53.MirrorCS");var subQ5=sQuery(id+"F37.wireOp",EDGE,"E94.0");var subQ6=sQuery(id+"F16.wireOp",EDGE,"E52.MirrorCS");Q5=makeQuery(id+"F46.boolean.opBoolean","SPLIT",EDGE,{"disambiguationData":[TD([makeQuery(id+"F17.opExtrude","SWEPT_FACE",FACE,{"disambiguationData":[OSD([subQ4])]})])],"derivedFrom":makeQuery(id+"F38.boolean.opBoolean","MERGE",EDGE,{"derivedFrom":[makeQuery(id+"F36.boolean.opBoolean","MERGE",EDGE,{"derivedFrom":[makeQuery(id+"F17.opExtrude","CAP_EDGE",EDGE,{"disambiguationData":[OSD([subQ6])],"isStart":true}),makeQuery(id+"F36.opPattern","COPY",EDGE,{"derivedFrom":makeQuery(id+"F35.opExtrude","SWEPT_EDGE",EDGE,{"disambiguationData":[OSD([subQ0,subQ2])]}),"instanceName":"1"})]}),makeQuery(id+"F38.opExtrude","SWEPT_EDGE",EDGE,{"disambiguationData":[OSD([subQ5,subQ1])]})]})});}
            fillet(context, id + "F47", {"entities" : qUnion([Q0, Q1, Q2, Q3, Q4, Q5]), "radius" : 1 * mm, "tangentPropagation" : true, "allowEdgeOverflow" : false});
        }
        {
            var Q0;
            {var subQ5=sQuery(id+"F37.wireOp",EDGE,"E92");var subQ8=sQuery(id+"F12.wireOp",EDGE,"E32.MirrorCS");var subQ14=makeQuery(id+"F35.opExtrude","SWEPT_FACE",FACE,{"disambiguationData":[OSD([sQuery(id+"F34.wireOp",EDGE,"E85")])]});Q0=makeQuery(id+"F42.boolean.opBoolean","SPLIT",FACE,{"disambiguationData":[TD([makeQuery(id+"F13.opExtrude","SWEPT_FACE",FACE,{"disambiguationData":[OSD([subQ8])]})])],"derivedFrom":makeQuery(id+"F38.boolean.opBoolean","MERGE",FACE,{"derivedFrom":[subQ14,makeQuery(id+"F36.opPattern","COPY",FACE,{"derivedFrom":subQ14,"instanceName":"1"}),makeQuery(id+"F38.opExtrude","SWEPT_FACE",FACE,{"disambiguationData":[OSD([subQ5])]})]})});}
            var sketch = newSketch(context, id + "F48", { "sketchPlane" : qUnion([Q0])});
            skLineSegment(sketch, "E120", {"start": v(35.5, -3.5) * mm, "end": v(35.5, -2.5) * mm});
            skLineSegment(sketch, "E121", {"start": v(35.5, -2.5) * mm, "end": v(25.5, -2.5) * mm});
            skLineSegment(sketch, "E122", {"start": v(25.5, -11.54) * mm, "end": v(25.5, -11.04) * mm, "construction": true});
            skLineSegment(sketch, "E123", {"start": v(25.5, -11.04) * mm, "end": v(33.91, -11.04) * mm});
            skLineSegment(sketch, "E124", {"start": v(33.91, -11.04) * mm, "end": v(35.5, -3.5) * mm});
            skLineSegment(sketch, "E125", {"start": v(25.5, -11.04) * mm, "end": v(25.5, -2.5) * mm});
            skSolve(sketch);
        }
        {
            var Q0;
            Q0 = qSketchRegion(id + "F48", true);
            extrude(context, id + "F49", {"entities" : qUnion([Q0]), "depth" : 1 * mm});
        }
        {
            var Q0;
            Q0=makeQuery(id+"F49.opExtrude","SWEPT_BODY",BODY,{"disambiguationData":[OSD([sQuery(id+"F48.wireOp",EDGE,"E120"),sQuery(id+"F48.wireOp",EDGE,"E121"),sQuery(id+"F48.wireOp",EDGE,"E123"),sQuery(id+"F48.wireOp",EDGE,"E124"),sQuery(id+"F48.wireOp",EDGE,"E125")])]});
            var Q1;
            Q1=qCreatedBy(makeId("Front.planeOp"),FACE);
            mirror(context, id + "F50", {"operationType" : NewBodyOperationType.ADD, "entities" : qUnion([Q0]), "mirrorPlane" : qUnion([Q1])});
        }
        {
            var Q0;
            Q0=makeQuery(id+"F49.opExtrude","CAP_EDGE",EDGE,{"disambiguationData":[OSD([sQuery(id+"F48.wireOp",EDGE,"E123")])],"isStart":true});
            var Q1;
            Q1=makeQuery(id+"F49.opExtrude","CAP_EDGE",EDGE,{"disambiguationData":[OSD([sQuery(id+"F48.wireOp",EDGE,"E125")])],"isStart":true});
            var Q2;
            Q2=makeQuery(id+"F50.opPattern","COPY",EDGE,{"derivedFrom":makeQuery(id+"F49.opExtrude","CAP_EDGE",EDGE,{"disambiguationData":[OSD([sQuery(id+"F48.wireOp",EDGE,"E123")])],"isStart":true}),"instanceName":"1"});
            var Q3;
            Q3=makeQuery(id+"F50.opPattern","COPY",EDGE,{"derivedFrom":makeQuery(id+"F49.opExtrude","CAP_EDGE",EDGE,{"disambiguationData":[OSD([sQuery(id+"F48.wireOp",EDGE,"E125")])],"isStart":true}),"instanceName":"1"});
            var Q4;
            {var subQ0=sQuery(id+"F20.wireOp",EDGE,"E58");Q4=makeQuery(id+"F40.boolean.opBoolean","INTERSECT",EDGE,{"derivedFrom":[makeQuery(id+"F38.boolean.opBoolean","MERGE",FACE,{"derivedFrom":[makeQuery(id+"F36.boolean.opBoolean","MERGE",FACE,{"derivedFrom":[makeQuery(id+"F21.boolean.opBoolean","COPY",FACE,{"derivedFrom":makeQuery(id+"F21.opExtrude","SWEPT_FACE",FACE,{"disambiguationData":[OSD([subQ0])]})}),makeQuery(id+"F35.opExtrude","SWEPT_FACE",FACE,{"disambiguationData":[OSD([subQ0,sQuery(id+"F34.wireOp",EDGE,"E83")])]})]}),makeQuery(id+"F38.opExtrude","SWEPT_FACE",FACE,{"disambiguationData":[OSD([sQuery(id+"F37.wireOp",EDGE,"E91")])]})]}),makeQuery(id+"F40.opExtrude","SWEPT_FACE",FACE,{"disambiguationData":[OSD([sQuery(id+"F39.wireOp",EDGE,"E100")])]})]});}
            var Q5;
            Q5=makeQuery(id+"F40.boolean.opBoolean","COPY",EDGE,{"derivedFrom":makeQuery(id+"F40.opExtrude","SWEPT_EDGE",EDGE,{"disambiguationData":[OSD([sQuery(id+"F16.wireOp",EDGE,"E47"),sQuery(id+"F34.wireOp",EDGE,"E82"),sQuery(id+"F34.wireOp",EDGE,"E87"),sQuery(id+"F37.wireOp",EDGE,"E90"),sQuery(id+"F37.wireOp",EDGE,"E96"),sQuery(id+"F39.wireOp",EDGE,"E100"),sQuery(id+"F39.wireOp",EDGE,"E103")])]})});
            var Q6;
            Q6=makeQuery(id+"F50.boolean.opBoolean","MERGE",EDGE,{"derivedFrom":[makeQuery(id+"F42.boolean.opBoolean","COPY",EDGE,{"derivedFrom":makeQuery(id+"F42.opExtrude","CAP_EDGE",EDGE,{"disambiguationData":[OSD([sQuery(id+"F41.wireOp",EDGE,"E109")])],"isStart":true})}),makeQuery(id+"F49.opExtrude","SWEPT_EDGE",EDGE,{"disambiguationData":[OSD([sQuery(id+"F48.wireOp",EDGE,"E120"),sQuery(id+"F48.wireOp",EDGE,"E121")])]})]});
            var Q7;
            Q7=makeQuery(id+"F50.boolean.opBoolean","MERGE",EDGE,{"derivedFrom":[makeQuery(id+"F42.boolean.opBoolean","COPY",EDGE,{"derivedFrom":makeQuery(id+"F42.opExtrude","CAP_EDGE",EDGE,{"disambiguationData":[OSD([sQuery(id+"F41.wireOp",EDGE,"E107")])],"isStart":true})}),makeQuery(id+"F50.opPattern","COPY",EDGE,{"derivedFrom":makeQuery(id+"F49.opExtrude","SWEPT_EDGE",EDGE,{"disambiguationData":[OSD([sQuery(id+"F48.wireOp",EDGE,"E120"),sQuery(id+"F48.wireOp",EDGE,"E121")])]}),"instanceName":"1"})]});
            var Q8;
            Q8=makeQuery(id+"F40.boolean.opBoolean","COPY",EDGE,{"derivedFrom":makeQuery(id+"F40.opExtrude","SWEPT_EDGE",EDGE,{"disambiguationData":[OSD([sQuery(id+"F16.wireOp",EDGE,"E52.MirrorCS"),sQuery(id+"F34.wireOp",EDGE,"E82"),sQuery(id+"F34.wireOp",EDGE,"E87"),sQuery(id+"F37.wireOp",EDGE,"E94.0"),sQuery(id+"F37.wireOp",EDGE,"E96"),sQuery(id+"F39.wireOp",EDGE,"E102"),sQuery(id+"F39.wireOp",EDGE,"E105")])]})});
            var Q9;
            Q9=makeQuery(id+"F40.boolean.opBoolean","INTERSECT",EDGE,{"derivedFrom":[makeQuery(id+"F38.boolean.opBoolean","MERGE",FACE,{"derivedFrom":[makeQuery(id+"F36.boolean.opBoolean","MERGE",FACE,{"derivedFrom":[makeQuery(id+"F26.boolean.opBoolean","COPY",FACE,{"derivedFrom":makeQuery(id+"F26.opExtrude","SWEPT_FACE",FACE,{"disambiguationData":[OSD([sQuery(id+"F25.wireOp",EDGE,"E64")])]})}),makeQuery(id+"F36.opPattern","COPY",FACE,{"derivedFrom":makeQuery(id+"F35.opExtrude","SWEPT_FACE",FACE,{"disambiguationData":[OSD([sQuery(id+"F20.wireOp",EDGE,"E58"),sQuery(id+"F34.wireOp",EDGE,"E83")])]}),"instanceName":"1"})]}),makeQuery(id+"F38.opExtrude","SWEPT_FACE",FACE,{"disambiguationData":[OSD([sQuery(id+"F37.wireOp",EDGE,"E95")])]})]}),makeQuery(id+"F40.opExtrude","SWEPT_FACE",FACE,{"disambiguationData":[OSD([sQuery(id+"F39.wireOp",EDGE,"E102")])]})]});
            var Q10;
            Q10=makeQuery(id+"F50.boolean.opBoolean","MERGE",EDGE,{"derivedFrom":[makeQuery(id+"F42.boolean.opBoolean","COPY",EDGE,{"derivedFrom":makeQuery(id+"F42.opExtrude","CAP_EDGE",EDGE,{"disambiguationData":[OSD([sQuery(id+"F41.wireOp",EDGE,"E107")])],"isStart":false})}),makeQuery(id+"F50.opPattern","COPY",EDGE,{"derivedFrom":makeQuery(id+"F49.opExtrude","SWEPT_EDGE",EDGE,{"disambiguationData":[OSD([sQuery(id+"F48.wireOp",EDGE,"E121"),sQuery(id+"F48.wireOp",EDGE,"E125")])]}),"instanceName":"1"})]});
            var Q11;
            Q11=makeQuery(id+"F50.boolean.opBoolean","MERGE",EDGE,{"derivedFrom":[makeQuery(id+"F42.boolean.opBoolean","COPY",EDGE,{"derivedFrom":makeQuery(id+"F42.opExtrude","CAP_EDGE",EDGE,{"disambiguationData":[OSD([sQuery(id+"F41.wireOp",EDGE,"E109")])],"isStart":false})}),makeQuery(id+"F49.opExtrude","SWEPT_EDGE",EDGE,{"disambiguationData":[OSD([sQuery(id+"F48.wireOp",EDGE,"E121"),sQuery(id+"F48.wireOp",EDGE,"E125")])]})]});
            fillet(context, id + "F51", {"entities" : qUnion([Q0, Q1, Q2, Q3, Q4, Q5, Q6, Q7, Q8, Q9, Q10, Q11]), "radius" : 0.5 * mm, "tangentPropagation" : true, "allowEdgeOverflow" : false});
        }
    });
